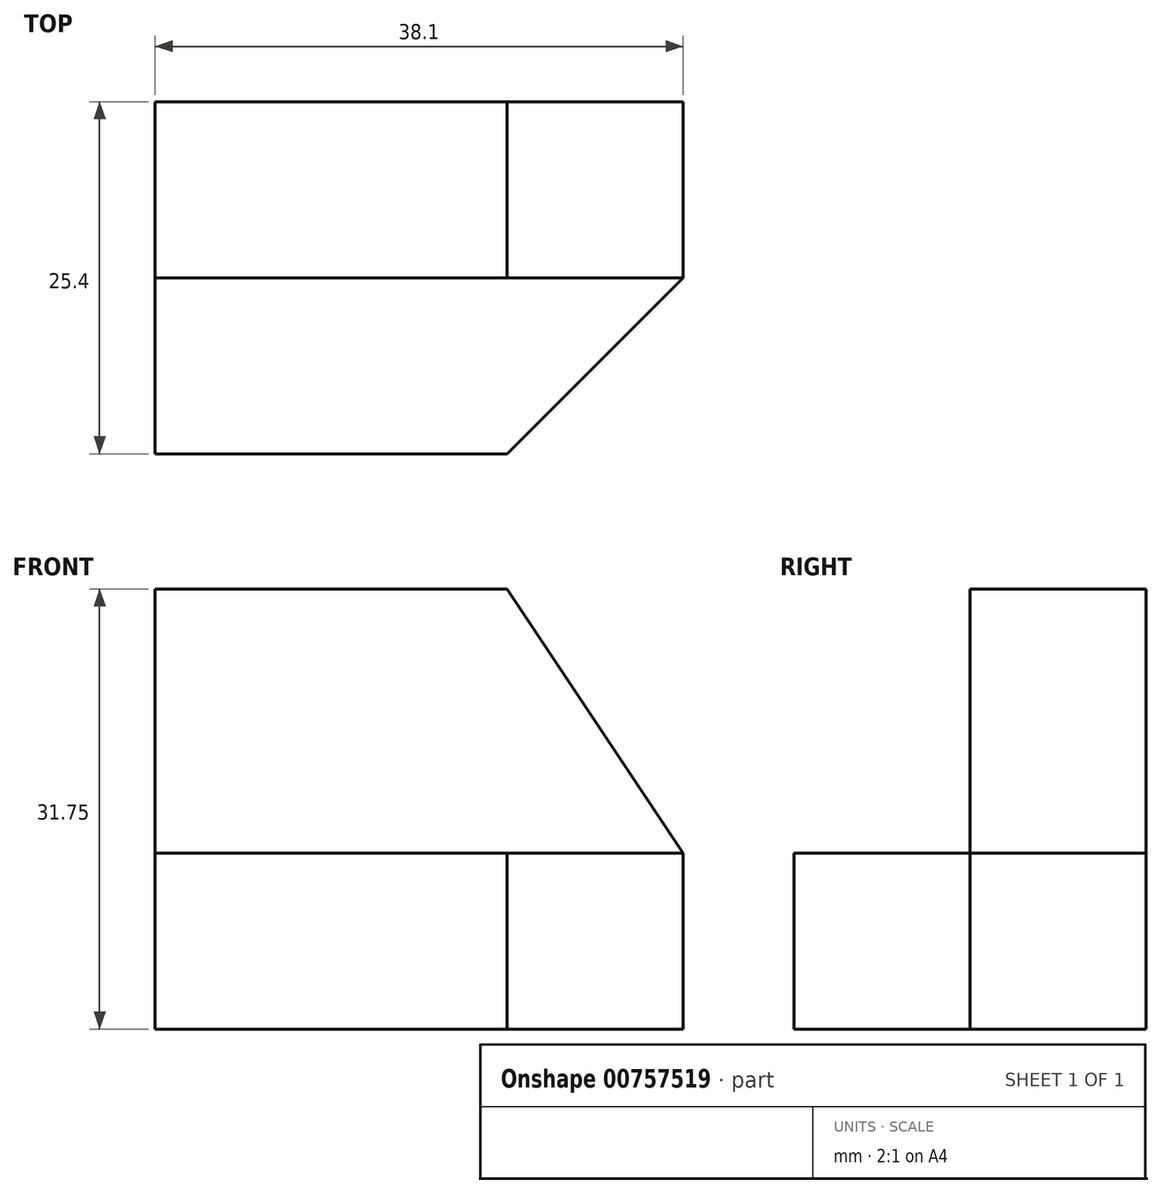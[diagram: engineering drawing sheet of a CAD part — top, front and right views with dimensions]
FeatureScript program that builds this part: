
annotation { "Feature Type Name" : "Feature", "Feature Type Description" : "" }
export const myFeature = defineFeature(function(context is Context, id is Id, definition is map)
    precondition{}
    {
        {
            var Q0;
            Q0=qCreatedBy(makeId("Front.planeOp"),FACE);
            var sketch = newSketch(context, id + "F0", { "sketchPlane" : qUnion([Q0])});
            skLineSegment(sketch, "E0", {"start": v(0, 0) * mm, "end": v(0, 31.75) * mm});
            skLineSegment(sketch, "E1", {"start": v(0, 31.75) * mm, "end": v(-38.1, 31.75) * mm});
            skLineSegment(sketch, "E2", {"start": v(-38.1, 31.75) * mm, "end": v(-38.1, 0) * mm});
            skLineSegment(sketch, "E3", {"start": v(-38.1, 0) * mm, "end": v(0, 0) * mm});
            skSolve(sketch);
        }
        {
            var Q0;
            Q0 = qSketchRegion(id + "F0", true);
            extrude(context, id + "F1", {"entities" : qUnion([Q0]), "depth" : 25.4 * mm, "offsetDistance" : 25.4 * mm});
        }
        {
            var Q0;
            Q0=makeQuery(id+"F1.opExtrude","SWEPT_FACE",FACE,{"disambiguationData":[OSD([sQuery(id+"F0.wireOp",EDGE,"E0")])]});
            var sketch = newSketch(context, id + "F2", { "sketchPlane" : qUnion([Q0])});
            skLineSegment(sketch, "E4", {"start": v(-12.7, 31.75) * mm, "end": v(-12.7, 12.7) * mm});
            skLineSegment(sketch, "E5", {"start": v(-12.7, 12.7) * mm, "end": v(-25.4, 12.7) * mm});
            skSolve(sketch);
        }
        {
            var Q0;
            {var subQ0=sQuery(id+"F2.wireOp",EDGE,"E4");Q0=makeQuery(id+"F2.imprint","IMPRINT",FACE,{"disambiguationData":[TD([[makeQuery(id+"F2.imprint","IMPRINT",EDGE,{"derivedFrom":subQ0}),-1.0]])]});}
            extrude(context, id + "F3", {"entities" : qUnion([Q0]), "operationType" : NewBodyOperationType.REMOVE, "endBound" : BoundingType.THROUGH_ALL, "oppositeDirection" : true, "depth" : 25.4 * mm, "offsetDistance" : 25.4 * mm});
        }
        {
            var Q0;
            Q0=makeQuery(id+"F3.boolean.opBoolean","COPY",FACE,{"derivedFrom":makeQuery(id+"F3.opExtrude","SWEPT_FACE",FACE,{"disambiguationData":[OSD([sQuery(id+"F2.wireOp",EDGE,"E4")])]})});
            var sketch = newSketch(context, id + "F4", { "sketchPlane" : qUnion([Q0])});
            skLineSegment(sketch, "E6", {"start": v(-12.7, 31.75) * mm, "end": v(0, 12.7) * mm});
            skSolve(sketch);
        }
        {
            var Q0;
            {var subQ0=sQuery(id+"F4.wireOp",EDGE,"E6");Q0=makeQuery(id+"F4.imprint","IMPRINT",FACE,{"disambiguationData":[TD([[makeQuery(id+"F4.imprint","IMPRINT",EDGE,{"derivedFrom":subQ0}),1.0]])]});}
            extrude(context, id + "F5", {"entities" : qUnion([Q0]), "operationType" : NewBodyOperationType.REMOVE, "endBound" : BoundingType.THROUGH_ALL, "oppositeDirection" : true, "depth" : 25.4 * mm, "offsetDistance" : 25.4 * mm});
        }
        {
            var Q0;
            Q0=makeQuery(id+"F3.boolean.opBoolean","COPY",FACE,{"derivedFrom":makeQuery(id+"F3.opExtrude","SWEPT_FACE",FACE,{"disambiguationData":[OSD([sQuery(id+"F2.wireOp",EDGE,"E5")])]})});
            var sketch = newSketch(context, id + "F6", { "sketchPlane" : qUnion([Q0])});
            skLineSegment(sketch, "E7", {"start": v(0, -12.7) * mm, "end": v(-12.7, -25.4) * mm});
            skSolve(sketch);
        }
        {
            var Q0;
            {var subQ0=sQuery(id+"F6.wireOp",EDGE,"E7");Q0=makeQuery(id+"F6.imprint","IMPRINT",FACE,{"disambiguationData":[TD([[makeQuery(id+"F6.imprint","IMPRINT",EDGE,{"derivedFrom":subQ0}),1.0]])]});}
            extrude(context, id + "F7", {"entities" : qUnion([Q0]), "operationType" : NewBodyOperationType.REMOVE, "endBound" : BoundingType.THROUGH_ALL, "oppositeDirection" : true, "depth" : 25.4 * mm, "offsetDistance" : 25.4 * mm});
        }
    });
